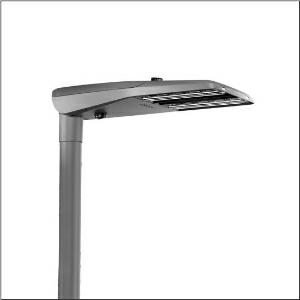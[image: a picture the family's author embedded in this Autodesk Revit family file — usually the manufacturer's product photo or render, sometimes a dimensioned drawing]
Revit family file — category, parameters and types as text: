
# Revit family: streetlight_sl_11_iq_midi___st1_0a_5xc3m51y08me_5fc7
name_source: partatom
category: Lighting Fixtures
units: mm (PartAtom-declared; Revit-internal decimal feet)

## family parameters
Cut with Voids When Loaded = No
Host = Face
Light Source = No
Part Type = Normal
Room Calculation Point = No
Round Connector Dimension = Use Diameter
Shared = No

## types (1)
- --- (1 x LED, 17540 lm, 122.7 W, 3000K)
    Apparent Load = 123 VA
    CIE Flux Codes = 33 66 96 100 100
    Color Rendering = 70
    Color Temperature = 3000K
    Default Elevation = 1800 mm
    Description = Streetlight SL 11 iQ midi, mast luminaire, primary light control with 3 zone facetted reflector, of plastic, silver coated, highly specular, primary optical cover: cover, of PMMA, transparent, light distribution: ST1.0a, light emission: direct distribution, primary light characteristic: asymmetric, installation type: post-top, side-entry, lamps: LED, High Power LED, rated values: 17.540lm | 122,7W | 143lm/W (begin service life); end service life: 17.540lm | 130,2W; at 50% lumin. flux: 8.770lm | 56,1W | 156,3lm/W, colour temperature: 3000K, colour rendering: CRI > 70, light colour: 730, light setting 1 begin service life: 100% | 17.540lm | 122,7W | 143lm/W | 3.000K, light setting 1 end service life: 130,2W, further light settings possible, control: pre-setting: logarithmic dimming characteristic, Street-Remote, Auto-Match, Temp-Guard, Lumen-Switch, Night-Set, Smart-Wire, Light-Fading, Desk-Remote (wireless, voltage-free reading and setting of iQ features in the workshop via application-optimized NFC function/RFID function), optimised constant luminous flux control (CLO 2.0), with cable H07RN-F 3x 1.5mm², mains connection: 230..240V, AC, 50/60Hz, connection cable pre-assembled, cable length: 12,5m, luminaire housing, of diecast aluminium, powder-coated, SITECO metallic grey (DB 702S), please order mast flange separately, inclination adjustable without tools: 0°, 5°, 10°, 15° (post-top) | 0°, -5°, -10°, -15° (side-entry), sealing non-destructively replaceable, multi-level sealing system, length: 780mm, width: 376mm, height: 118mm, mast flange for spigot size: 42mm (side-entry): 5XC10008XM4, 60/48mm (side-entry/post-top): 5XC10108XM2, 76/60mm (side-entry/post-top): 5XC10108XM1, equipment: Power, Smart Interface below and above, protection rating (complete): IP66, insulation class (complete): insulation class II (safety insulation), certification: CE, ENEC, ENEC+, VDE, UKCA, impact resistance: IK10, permissible operating ambient temperature for outdoor applications: -25..+50°C, standard-compliant lighting for roads and squares, Environmental Product Declaration (EPD) tested and certified by an independent institute, packaging unit: 1 piece

Light Distribution: ST1.0a
    Height = 118 mm
    Lamp = 1 x LED
    Lamp Light Flux = 17540 lm
    Lamp Power = 122.7 W
    Lamp count = 1
    Length = 780 mm
    Luminous efficacy = 143 lm/W
    Manufacturer = Siteco
    ModVariant = No
    Model = 5XC3M51Y08ME
    Number of Poles = 1
    OnlyDefault = Yes
    Power Factor = 1
    Product Name = Streetlight SL 11 iQ midi | ST1.0a
    Product group = mast luminaire | pylon top
    ProductGroupID = 6100
    Protection Class = Protection class II
    Protection Degree = IP 66
    RLX_Detail_Level = 1
    RLX_Emergency_Light_Flux = 0 lm
    RLX_Emergency_Type = 0
    RLX_Emergency_Type_DB = No
    RlxData = <blob elided: 69549 chars, md5=87a656d8>
    Socket = socket
    Standby Power = 0 W
    System Light Flux = 17540 lm
    System Power = 123 W
    Type Comments = factory setting: luminous flux: 100 % | dim-lin: 254 | 553 mA
    Type Image = l_1004429.jpg
    URL = http://relux.com
    VarID = @adj_092265
    Voltage = 0 V
    Weight = 0.00 kg
    Width = 376 mm

## geometry (parser evidence)
native form markers: Blend x4, Sweep x10
no freeform markers — native parametric forms only
